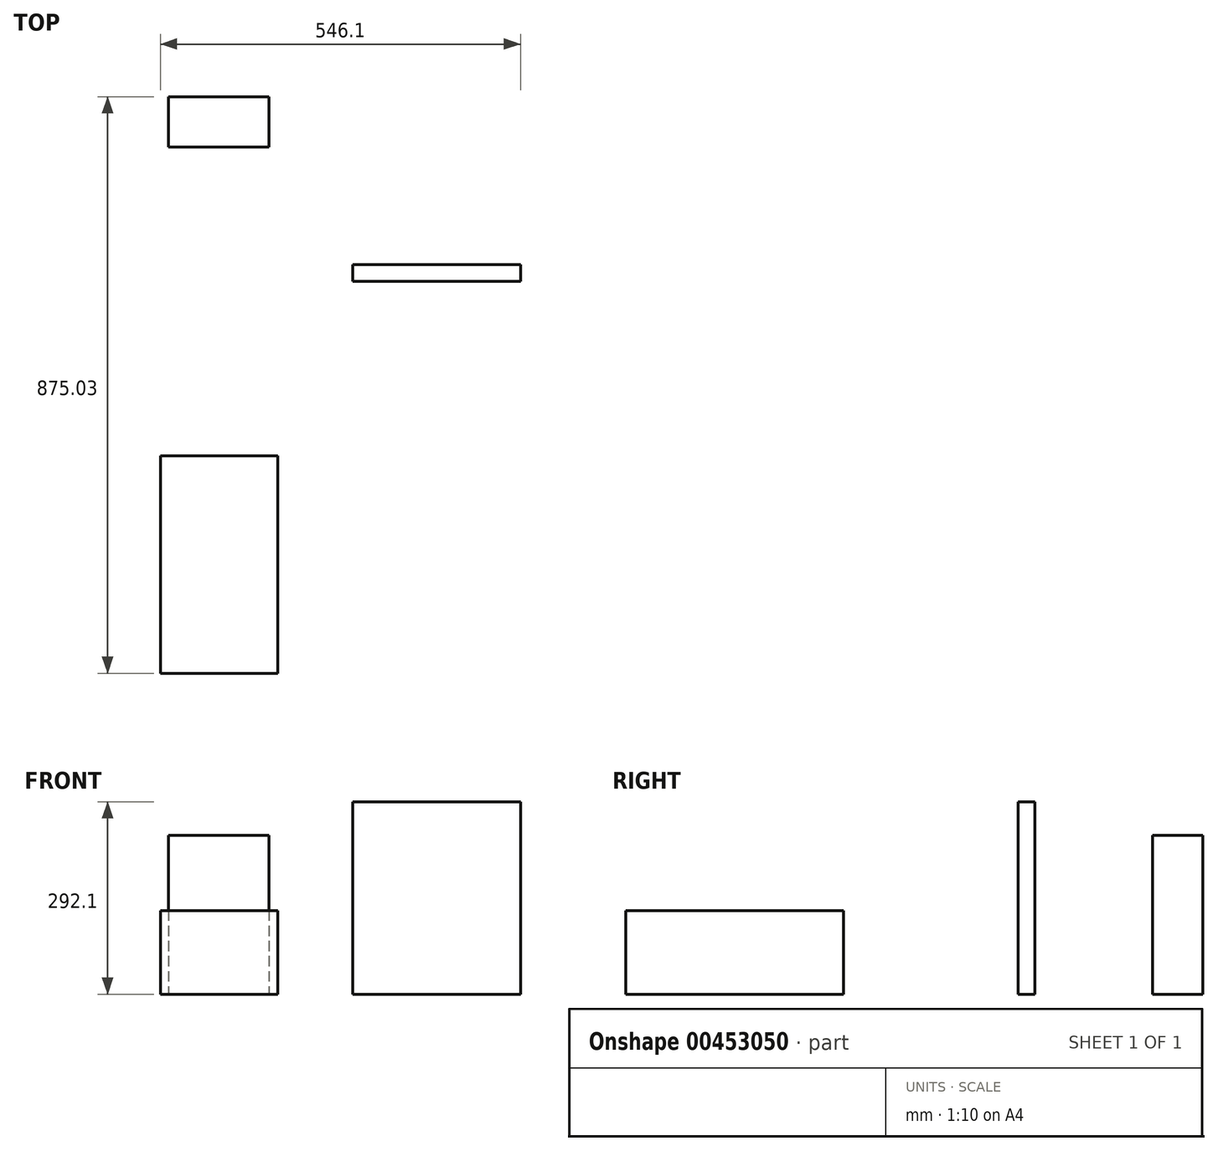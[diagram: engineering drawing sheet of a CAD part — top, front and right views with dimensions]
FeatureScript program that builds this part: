
annotation { "Feature Type Name" : "Feature", "Feature Type Description" : "" }
export const myFeature = defineFeature(function(context is Context, id is Id, definition is map)
    precondition{}
    {
        {
            var Q0;
            Q0=qCreatedBy(makeId("Top.planeOp"),FACE);
            var sketch = newSketch(context, id + "F0", { "sketchPlane" : qUnion([Q0])});
            skLineSegment(sketch, "E0.bottom", {"start": v(-76.2, 38.1) * mm, "end": v(76.2, 38.1) * mm});
            skLineSegment(sketch, "E0.top", {"start": v(-76.2, -38.1) * mm, "end": v(76.2, -38.1) * mm});
            skLineSegment(sketch, "E0.left", {"start": v(-76.2, 38.1) * mm, "end": v(-76.2, -38.1) * mm});
            skLineSegment(sketch, "E0.right", {"start": v(76.2, 38.1) * mm, "end": v(76.2, -38.1) * mm});
            skPoint(sketch, "E0.middle", {"position": v(0, 0) * mm});
            skSolve(sketch);
        }
        {
            var Q0;
            Q0 = qSketchRegion(id + "F0", true);
            extrude(context, id + "F1", {"entities" : qUnion([Q0]), "depth" : 241.3 * mm, "offsetDistance" : 25.4 * mm});
        }
        {
            var Q0;
            Q0=makeQuery(id+"F1.opExtrude","SWEPT_BODY",BODY,{"disambiguationData":[OSD([sQuery(id+"F0.wireOp",EDGE,"E0.bottom"),sQuery(id+"F0.wireOp",EDGE,"E0.top"),sQuery(id+"F0.wireOp",EDGE,"E0.left"),sQuery(id+"F0.wireOp",EDGE,"E0.right")])]});
            transform(context, id + "F2", {"entities" : qUnion([Q0]), "transformType" : TransformType.TRANSLATION_3D, "dx" : 0 * mm, "dy" : 220.98 * mm, "dz" : 0 * mm, "makeCopy" : false});
        }
        {
            var Q0;
            Q0=qCreatedBy(makeId("Top.planeOp"),FACE);
            var sketch = newSketch(context, id + "F3", { "sketchPlane" : qUnion([Q0])});
            skLineSegment(sketch, "E1.bottom", {"start": v(127, -21.42) * mm, "end": v(-127, -21.42) * mm});
            skLineSegment(sketch, "E1.top", {"start": v(127, 3.98) * mm, "end": v(-127, 3.98) * mm});
            skLineSegment(sketch, "E1.left", {"start": v(127, -21.42) * mm, "end": v(127, 3.98) * mm});
            skLineSegment(sketch, "E1.right", {"start": v(-127, -21.42) * mm, "end": v(-127, 3.98) * mm});
            skPoint(sketch, "E1.middle", {"position": v(0, -8.72) * mm});
            skSolve(sketch);
        }
        {
            var Q0;
            Q0 = qSketchRegion(id + "F3", true);
            extrude(context, id + "F4", {"entities" : qUnion([Q0]), "depth" : 292.1 * mm, "offsetDistance" : 25.4 * mm});
        }
        {
            var Q0;
            Q0=makeQuery(id+"F4.opExtrude","SWEPT_BODY",BODY,{"disambiguationData":[OSD([sQuery(id+"F3.wireOp",EDGE,"E1.bottom"),sQuery(id+"F3.wireOp",EDGE,"E1.top"),sQuery(id+"F3.wireOp",EDGE,"E1.left"),sQuery(id+"F3.wireOp",EDGE,"E1.right")])]});
            transform(context, id + "F5", {"entities" : qUnion([Q0]), "transformType" : TransformType.TRANSLATION_3D, "dx" : 330.2 * mm, "dy" : 0 * mm, "dz" : 0 * mm, "makeCopy" : false});
        }
        {
            var Q0;
            Q0=qCreatedBy(makeId("Top.planeOp"),FACE);
            var sketch = newSketch(context, id + "F6", { "sketchPlane" : qUnion([Q0])});
            skLineSegment(sketch, "E2.bottom", {"start": v(88.9, -165.1) * mm, "end": v(-88.9, -165.1) * mm});
            skLineSegment(sketch, "E2.top", {"start": v(88.9, 165.1) * mm, "end": v(-88.9, 165.1) * mm});
            skLineSegment(sketch, "E2.left", {"start": v(88.9, -165.1) * mm, "end": v(88.9, 165.1) * mm});
            skLineSegment(sketch, "E2.right", {"start": v(-88.9, -165.1) * mm, "end": v(-88.9, 165.1) * mm});
            skPoint(sketch, "E2.middle", {"position": v(0, 0) * mm});
            skSolve(sketch);
        }
        {
            var Q0;
            Q0 = qSketchRegion(id + "F6", true);
            extrude(context, id + "F7", {"entities" : qUnion([Q0]), "depth" : 127 * mm, "offsetDistance" : 25.4 * mm});
        }
        {
            var Q0;
            Q0=makeQuery(id+"F7.opExtrude","SWEPT_BODY",BODY,{"disambiguationData":[OSD([sQuery(id+"F6.wireOp",EDGE,"E2.bottom"),sQuery(id+"F6.wireOp",EDGE,"E2.top"),sQuery(id+"F6.wireOp",EDGE,"E2.left"),sQuery(id+"F6.wireOp",EDGE,"E2.right")])]});
            transform(context, id + "F8", {"entities" : qUnion([Q0]), "transformType" : TransformType.TRANSLATION_3D, "dx" : 0 * mm, "dy" : -450.85 * mm, "dz" : 0 * mm, "makeCopy" : false});
        }
    });
